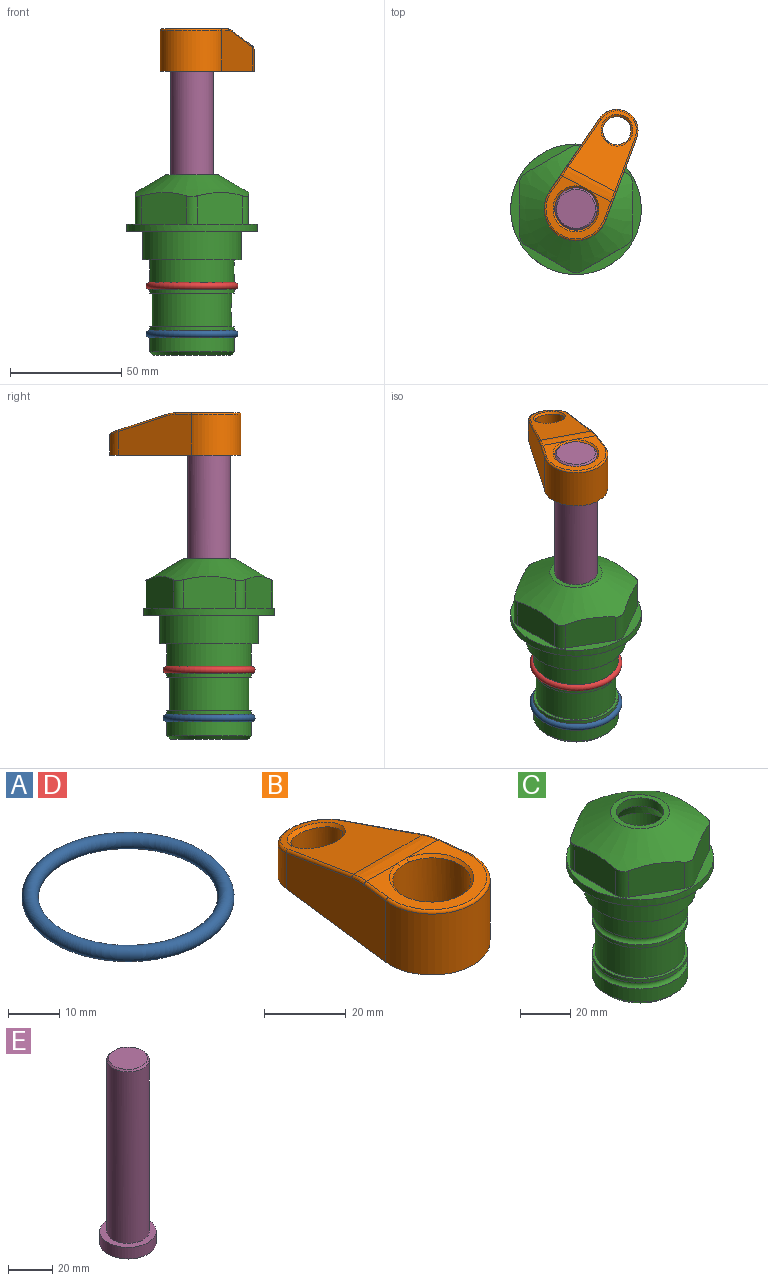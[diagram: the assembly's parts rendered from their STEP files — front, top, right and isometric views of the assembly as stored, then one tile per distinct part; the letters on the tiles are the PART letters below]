
ASSEMBLY  parts=5 mates=4
PART A: 1 faces, bbox 44.7x44.7x3.2 mm
  f0: torus R=19.05mm, axis (0,0,1), area 1193.9mm2
PART B: 31 faces, bbox 31.7x65.5x19.8 mm
  f0: plane 39.12x18.26mm, normal (0.99,0.12,0), area 612.2mm2, adj f1,f4,f7,f11,f13,f15
  f1: cylinder r=9.53mm len=18.91mm, axis (0,0,-1), area 296.1mm2, adj f0,f2,f7,f17
  f2: plane 39.12x18.26mm, normal (-0.99,0.12,0), area 612.2mm2, adj f1,f4,f7,f12,f14,f16
  f3: cylinder r=6.35mm len=12.7mm, axis (0,0,-1), area 362.4mm2, adj f7,f18
  f4: cylinder r=14.29mm len=28.58mm, axis (0,0,-1), area 882.2mm2, adj f0,f2,f7,f10
  f5: cylinder r=9.53mm len=19.05mm, axis (0,0,-1), area 1092.6mm2, adj f7,f19,f20
  f6: plane 26.99x23.69mm, normal (0,0,1), area 216.2mm2, adj f9,f10,f11,f12,f19
  f7: plane 63.5x28.58mm, normal (0,0,-1), area 661.8mm2, adj f0,f1,f2,f3,f4,f5,f22,f23
  f8: plane 33.52x23.6mm, normal (0,0.26,0.97), area 486mm2, adj f9,f15,f16,f17,f18
  f9: cylinder r=19.05mm len=24.72mm, axis (1,0,0), area 120.4mm2, adj f6,f8,f13,f14,f20
  f10: torus R=13.49mm, axis (0,0,1), area 59mm2, adj f4,f6,f11,f12
  f11: cylinder r=0.79mm len=8.67mm, axis (0.12,-0.99,0), area 10.8mm2, adj f0,f6,f10,f13
  f12: cylinder r=0.79mm len=8.67mm, axis (0.12,0.99,0), area 10.8mm2, adj f2,f6,f10,f14
  f13: bspline ~4.95x1.42mm, area 6.1mm2, adj f0,f9,f11,f15
  f14: bspline ~4.95x1.42mm, area 6.1mm2, adj f2,f9,f12,f16
  f15: cylinder r=0.79mm len=25.95mm, axis (0.12,-0.96,0.26), area 32.9mm2, adj f0,f8,f13,f17
  f16: cylinder r=0.79mm len=25.95mm, axis (0.12,0.96,-0.26), area 32.9mm2, adj f2,f8,f14,f17
  f17: bspline ~18.91x8.38mm, area 30mm2, adj f1,f8,f15,f16
  f18: bspline ~14.29x14.29mm, area 48.3mm2, adj f3,f8
  f19: cone r=9.53mm half-angle=45deg, axis (0,0,1), area 66.5mm2, adj f5,f6,f20
  f20: bspline ~3.22x0.96mm, area 3.5mm2, adj f5,f9,f19
  f21: plane 2.75x2.72mm, normal (0,0,-1), area 2.9mm2, adj f23,f25,f28
  f22: plane 23.05x15.88mm, normal (-0.99,-0.12,0), area 323.6mm2, adj f7,f25,f26,f27,f28,f29
  f23: plane 23.05x15.88mm, normal (0.99,-0.12,0), area 323.6mm2, adj f7,f21,f25,f27,f28,f30
  f24: cylinder r=9.53mm len=10.69mm, axis (0,0,-1), area 114.7mm2, adj f7,f27,f29,f30
  f25: cylinder r=12.7mm len=20.59mm, axis (0,0,-1), area 381.1mm2, adj f7,f21,f22,f23,f26,f28
  f26: plane 2.75x2.72mm, normal (0,0,-1), area 2.9mm2, adj f22,f25,f28
  f27: plane 19.72x18.37mm, normal (0,-0.26,-0.97), area 291.8mm2, adj f22,f23,f24,f28,f29,f30
  f28: cylinder r=15.88mm len=19.92mm, axis (1,0,0), area 54.8mm2, adj f21,f22,f23,f25,f26,f27
  f29: cylinder r=1.59mm len=11mm, axis (0,0,-1), area 34.7mm2, adj f7,f22,f24,f27
  f30: cylinder r=1.59mm len=11mm, axis (0,0,-1), area 34.7mm2, adj f7,f23,f24,f27
PART C: 36 faces, bbox 58.7x58.7x81 mm
  f0: cylinder r=17.78mm len=35.56mm, axis (0,0,1), area 1670.8mm2, adj f23,f24,f31
  f1: cylinder r=19.05mm len=38.1mm, axis (0,0,1), area 1191.9mm2, adj f26,f27,f30
  f2: plane 58.66x58.66mm, normal (0,0,-1), area 1150.6mm2, adj f3,f28
  f3: cylinder r=29.33mm len=58.66mm, axis (0,0,-1), area 585.1mm2, adj f2,f4
  f4: plane 58.66x58.66mm, normal (0,0,1), area 475.9mm2, adj f3,f5,f6,f7,f8,f9,f10,f11
  f5: plane 20.32x14.34mm, normal (-0.5,0.87,0), area 324.4mm2, adj f4,f15,f16,f17
  f6: plane 20.32x14.34mm, normal (0.5,0.87,0), area 324.4mm2, adj f4,f14,f15,f17
  f7: plane 23.48x14.34mm, normal (1,0,0), area 324.4mm2, adj f4,f13,f14,f17
  f8: plane 20.32x14.34mm, normal (0.5,-0.87,0), area 324.4mm2, adj f4,f12,f13,f17
  f9: plane 20.32x14.34mm, normal (-0.5,-0.87,0), area 324.4mm2, adj f4,f11,f12,f17
  f10: plane 23.48x14.34mm, normal (-1,0,0), area 324.4mm2, adj f4,f11,f16,f17
  f11: cylinder r=5.08mm len=12.85mm, axis (0,0,-1), area 67.2mm2, adj f4,f9,f10,f17
  f12: cylinder r=5.08mm len=12.85mm, axis (0,0,-1), area 67.2mm2, adj f4,f8,f9,f17
  f13: cylinder r=5.08mm len=12.85mm, axis (0,0,-1), area 67.2mm2, adj f4,f7,f8,f17
  f14: cylinder r=5.08mm len=12.85mm, axis (0,0,-1), area 67.2mm2, adj f4,f6,f7,f17
  f15: cylinder r=5.08mm len=12.85mm, axis (0,0,-1), area 67.2mm2, adj f4,f5,f6,f17
  f16: cylinder r=5.08mm len=12.85mm, axis (0,0,-1), area 67.2mm2, adj f4,f5,f10,f17
  f17: cone r=11.73mm half-angle=60deg, axis (0,0,-1), area 2071.8mm2, adj f5,f6,f7,f8,f9,f10,f11,f12
  f18: plane 23.46x23.46mm, normal (0,0,1), area 147.4mm2, adj f17,f35
  f19: plane 34.93x34.93mm, normal (0,0,-1), area 958mm2, adj f29
  f20: cylinder r=19.05mm len=38.1mm, axis (0,0,1), area 760.1mm2, adj f21,f29
  f21: torus R=19.05mm, axis (0,0,1), area 565.3mm2, adj f20,f22
  f22: cylinder r=19.05mm len=38.1mm, axis (0,0,1), area 190mm2, adj f21,f23
  f23: plane 38.1x38.1mm, normal (0,0,1), area 146.9mm2, adj f0,f22
  f24: plane 38.1x38.1mm, normal (0,0,-1), area 146.9mm2, adj f0,f25
  f25: cylinder r=19.05mm len=38.1mm, axis (0,0,1), area 190mm2, adj f24,f26
  f26: torus R=19.05mm, axis (0,0,1), area 565.3mm2, adj f1,f25
  f27: plane 44.45x44.45mm, normal (0,0,-1), area 411.7mm2, adj f1,f28
  f28: cylinder r=22.23mm len=44.45mm, axis (0,0,1), area 1773.5mm2, adj f2,f27
  f29: cone r=19.05mm half-angle=45deg, axis (0,0,1), area 257.5mm2, adj f19,f20
  f30: cylinder r=3.17mm len=6.75mm, axis (-1,0,0), area 128mm2, adj f1,f33
  f31: cylinder r=3.17mm len=6.35mm, axis (-1,0,0), area 102.5mm2, adj f0,f33
  f32: plane 25.4x25.4mm, normal (0,0,1), area 506.7mm2, adj f33
  f33: cylinder r=12.7mm len=66.42mm, axis (0,0,-1), area 5236.2mm2, adj f30,f31,f32,f34
  f34: cone r=9.53mm half-angle=30deg, axis (0,0,-1), area 443.4mm2, adj f33,f35
  f35: cylinder r=9.53mm len=19.05mm, axis (0,0,-1), area 240.9mm2, adj f18,f34
PART D: same geometry as A
PART E: 6 faces, bbox 25.4x25.4x101.6 mm
  f0: plane 17.46x17.46mm, normal (0,0,1), area 239.5mm2, adj f5
  f1: plane 25.4x25.4mm, normal (0,0,-1), area 506.7mm2, adj f2
  f2: cylinder r=12.7mm len=25.4mm, axis (0,0,1), area 506.7mm2, adj f1,f3
  f3: plane 25.4x25.4mm, normal (0,0,1), area 221.7mm2, adj f2,f4
  f4: cylinder r=9.53mm len=94.46mm, axis (0,0,1), area 5653mm2, adj f3,f5
  f5: cone r=8.73mm half-angle=45deg, axis (0,0,-1), area 64.4mm2, adj f0,f4
PLACE A t=(0,0,-21.59)mm
PLACE B rot(axis=(0,0,-1),27.6deg) t=(0,0,27.55)mm
PLACE C at identity fixed
PLACE D at identity
PLACE E rot(axis=(0,0,-1),27.6deg) t=(0,0,27.55)mm
MATE fastened A.f0 <-> C.f0  axis (0,0,1) through (0,0,-46.1)mm
MATE fastened B.f4 <-> E.f2  axis (0,0,1) through (0,0,91.05)mm
MATE fastened D.f0 <-> C.f0  axis (0,0,1) through (0,0,-24.51)mm
MATE cylindrical C.f0 <-> E.f2  axis (0,0,1) through (0,0,-50.55)mm
